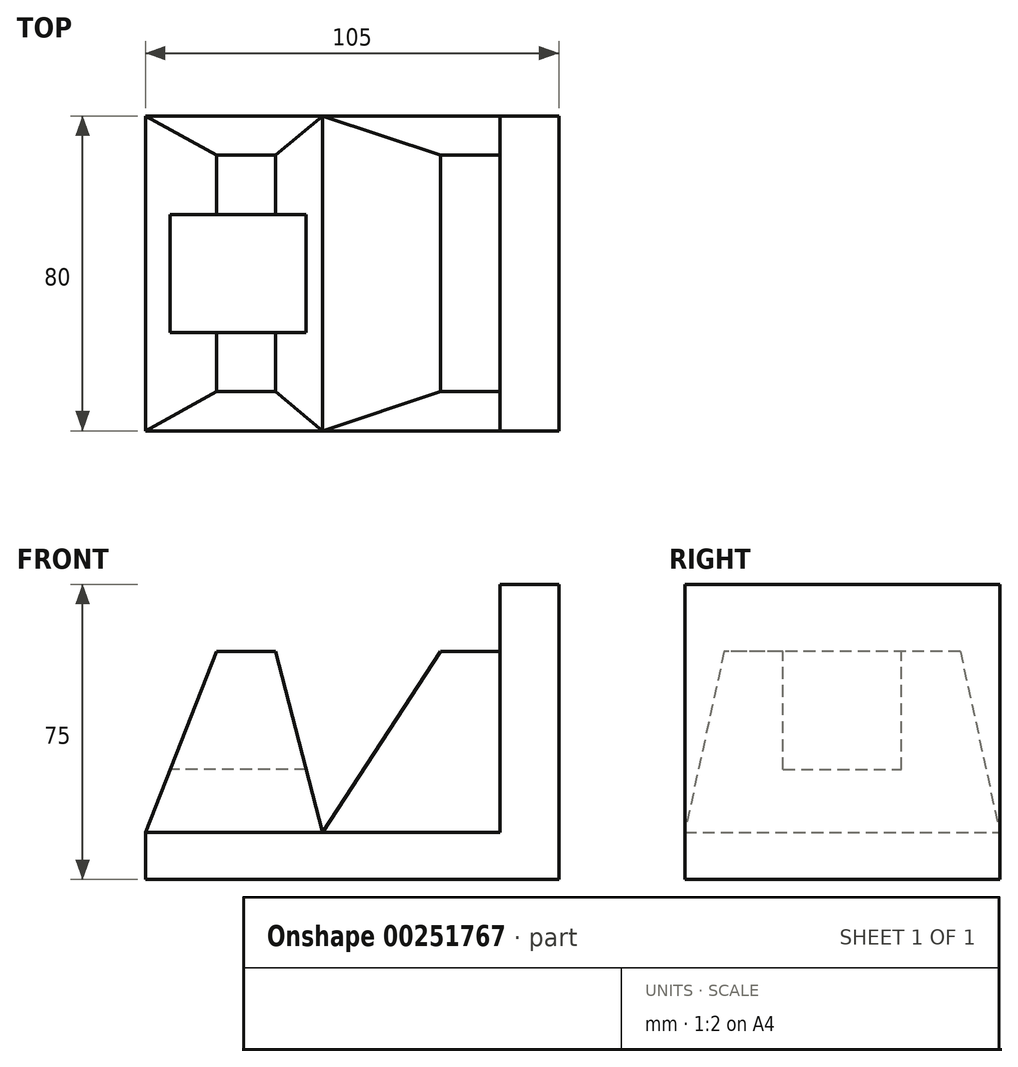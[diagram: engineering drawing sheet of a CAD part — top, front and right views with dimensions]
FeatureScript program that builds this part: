
annotation { "Feature Type Name" : "Feature", "Feature Type Description" : "" }
export const myFeature = defineFeature(function(context is Context, id is Id, definition is map)
    precondition{}
    {
        {
            var Q0;
            Q0=qCreatedBy(makeId("Front.planeOp"),FACE);
            var sketch = newSketch(context, id + "F0", { "sketchPlane" : qUnion([Q0])});
            skLineSegment(sketch, "E0.bottom", {"start": v(52.5, -6) * mm, "end": v(-52.5, -6) * mm});
            skLineSegment(sketch, "E0.top", {"start": v(52.5, 6) * mm, "end": v(-52.5, 6) * mm});
            skLineSegment(sketch, "E0.left", {"start": v(52.5, -6) * mm, "end": v(52.5, 6) * mm});
            skLineSegment(sketch, "E0.right", {"start": v(-52.5, -6) * mm, "end": v(-52.5, 6) * mm});
            skPoint(sketch, "E0.middle", {"position": v(0, 0) * mm});
            skLineSegment(sketch, "E1.bottom", {"start": v(52.5, 6) * mm, "end": v(37.5, 6) * mm});
            skLineSegment(sketch, "E1.top", {"start": v(52.5, 69) * mm, "end": v(37.5, 69) * mm});
            skLineSegment(sketch, "E1.left", {"start": v(52.5, 6) * mm, "end": v(52.5, 69) * mm});
            skLineSegment(sketch, "E1.right", {"start": v(37.5, 6) * mm, "end": v(37.5, 69) * mm});
            skSolve(sketch);
        }
        {
            var Q0;
            Q0 = qSketchRegion(id + "F0", true);
            extrude(context, id + "F1", {"entities" : qUnion([Q0]), "endBound" : BoundingType.SYMMETRIC, "depth" : 80 * mm});
        }
        {
            var Q0;
            Q0=makeQuery(id+"F1.opExtrude","SWEPT_FACE",FACE,{"disambiguationData":[OSD([sQuery(id+"F0.wireOp",EDGE,"E0.top")])]});
            var sketch = newSketch(context, id + "F2", { "sketchPlane" : qUnion([Q0])});
            skLineSegment(sketch, "E2.bottom", {"start": v(-52.5, 40) * mm, "end": v(-7.5, 40) * mm});
            skLineSegment(sketch, "E2.top", {"start": v(-52.5, -40) * mm, "end": v(-7.5, -40) * mm});
            skLineSegment(sketch, "E2.left", {"start": v(-52.5, 40) * mm, "end": v(-52.5, -40) * mm});
            skLineSegment(sketch, "E2.right", {"start": v(-7.5, 40) * mm, "end": v(-7.5, -40) * mm});
            skSolve(sketch);
        }
        {
            var Q0;
            Q0=qCreatedBy(makeId("Top.planeOp"),FACE);
            cPlane(context, id + "F3", {"entities" : qUnion([Q0]), "cplaneType" : CPlaneType.OFFSET, "offset" : 52 * mm, "width" : 150 * mm, "height" : 150 * mm});
        }
        {
            var Q0;
            Q0=qCreatedBy(id+"F3.planeOp",FACE);
            var sketch = newSketch(context, id + "F4", { "sketchPlane" : qUnion([Q0])});
            skLineSegment(sketch, "E3.bottom", {"start": v(-34.5, 30) * mm, "end": v(-19.5, 30) * mm});
            skLineSegment(sketch, "E3.top", {"start": v(-34.5, -30) * mm, "end": v(-19.5, -30) * mm});
            skLineSegment(sketch, "E3.left", {"start": v(-34.5, 30) * mm, "end": v(-34.5, -30) * mm});
            skLineSegment(sketch, "E3.right", {"start": v(-19.5, 30) * mm, "end": v(-19.5, -30) * mm});
            skLineSegment(sketch, "E4.bottom", {"start": v(22.5, 30) * mm, "end": v(37.5, 30) * mm});
            skLineSegment(sketch, "E4.top", {"start": v(22.5, -30) * mm, "end": v(37.5, -30) * mm});
            skLineSegment(sketch, "E4.left", {"start": v(22.5, 30) * mm, "end": v(22.5, -30) * mm});
            skLineSegment(sketch, "E4.right", {"start": v(37.5, 30) * mm, "end": v(37.5, -30) * mm});
            skSolve(sketch);
        }
        {
            var Q1;
            Q1=makeQuery(id+"F4.imprint","IMPRINT",FACE,{"disambiguationData":[TD([[makeQuery(id+"F4.imprint","IMPRINT",EDGE,{"derivedFrom":sQuery(id+"F4.wireOp",EDGE,"E3.bottom")}),-1.0]])]});
            var Q2;
            Q2=makeQuery(id+"F2.imprint","IMPRINT",FACE,{"disambiguationData":[TD([[makeQuery(id+"F2.imprint","IMPRINT",EDGE,{"derivedFrom":sQuery(id+"F2.wireOp",EDGE,"E2.bottom")}),1.0]])]});
            loft(context, id + "F5", {"operationType" : NewBodyOperationType.ADD, "sheetProfilesArray" : [{ "sheetProfileEntities" : qUnion([Q1]) }, { "sheetProfileEntities" : qUnion([Q2]) }]});
        }
        {
            var Q1;
            Q1=makeQuery(id+"F4.imprint","IMPRINT",FACE,{"disambiguationData":[TD([[makeQuery(id+"F4.imprint","IMPRINT",EDGE,{"derivedFrom":sQuery(id+"F4.wireOp",EDGE,"E4.bottom")}),-1.0]])]});
            var Q2;
            Q2=makeQuery(id+"F1.opExtrude","SWEPT_FACE",FACE,{"disambiguationData":[OSD([sQuery(id+"F0.wireOp",EDGE,"E0.top")])]});
            loft(context, id + "F6", {"operationType" : NewBodyOperationType.ADD, "sheetProfilesArray" : [{ "sheetProfileEntities" : qUnion([Q1]) }, { "sheetProfileEntities" : qUnion([Q2]) }]});
        }
        {
            var Q0;
            Q0=qCreatedBy(makeId("Right.planeOp"),FACE);
            cPlane(context, id + "F7", {"entities" : qUnion([Q0]), "cplaneType" : CPlaneType.OFFSET, "offset" : 52.5 * mm, "oppositeDirection" : true, "width" : 150 * mm, "height" : 150 * mm});
        }
        {
            var Q0;
            Q0=qCreatedBy(id+"F7.planeOp",FACE);
            var sketch = newSketch(context, id + "F8", { "sketchPlane" : qUnion([Q0])});
            skLineSegment(sketch, "E5.bottom", {"start": v(15, 52) * mm, "end": v(-15, 52) * mm});
            skLineSegment(sketch, "E5.top", {"start": v(15, 22) * mm, "end": v(-15, 22) * mm});
            skLineSegment(sketch, "E5.left", {"start": v(15, 52) * mm, "end": v(15, 22) * mm});
            skLineSegment(sketch, "E5.right", {"start": v(-15, 52) * mm, "end": v(-15, 22) * mm});
            skSolve(sketch);
        }
        {
            var Q0;
            Q0 = qSketchRegion(id + "F8", true);
            extrude(context, id + "F9", {"entities" : qUnion([Q0]), "operationType" : NewBodyOperationType.REMOVE, "depth" : 50 * mm});
        }
    });
